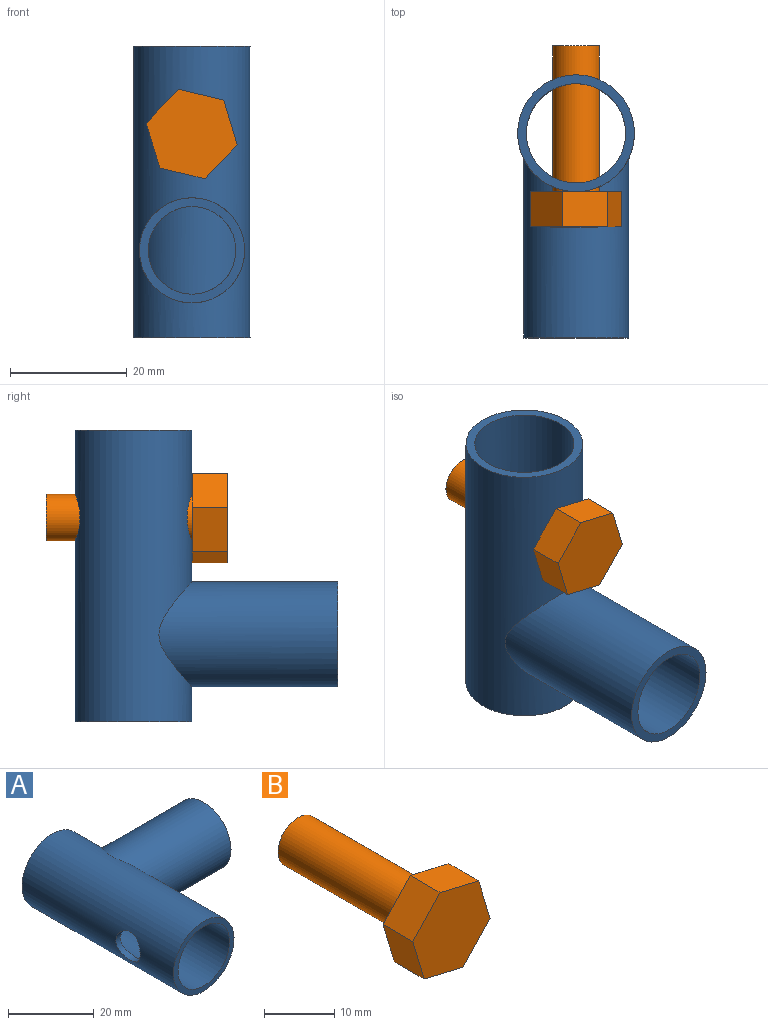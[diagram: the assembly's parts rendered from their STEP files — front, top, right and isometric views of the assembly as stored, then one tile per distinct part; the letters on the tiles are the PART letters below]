
ASSEMBLY  parts=2 mates=1
PART A: 10 faces, bbox 45x50x20 mm
  f0: cylinder r=10mm len=50mm, axis (0,1,0), area 2744.7mm2, adj f2,f3,f5,f8,f9
  f1: cylinder r=8.5mm len=50mm, axis (0,1,0), area 2566.7mm2, adj f2,f3,f8,f9
  f2: plane 20x20mm, normal (0,-1,0), area 87.2mm2, adj f0,f1
  f3: plane 20x20mm, normal (0,1,0), area 87.2mm2, adj f0,f1
  f4: plane 18x18mm, normal (1,0,0), area 77.8mm2, adj f5,f6
  f5: cylinder r=9mm len=30.66mm, axis (-1,0,0), area 1558.3mm2, adj f0,f4
  f6: cylinder r=7.5mm len=28.4mm, axis (-1,0,0), area 1254.3mm2, adj f4,f7
  f7: cylinder r=10mm len=15mm, axis (0,1,0), area 193mm2, adj f6
  f8: cylinder r=4mm len=8mm, axis (1,0,0), area 39.3mm2, adj f0,f1
  f9: cylinder r=4mm len=8mm, axis (1,0,0), area 40mm2, adj f0,f1
PART B: 10 faces, bbox 15.6x31x15.3 mm
  f0: plane 7.67x6mm, normal (0.96,0,0.29), area 48mm2, adj f1,f5,f6,f7
  f1: plane 7.78x6mm, normal (0.23,0,0.97), area 48mm2, adj f0,f2,f6,f7
  f2: plane 6x5.81mm, normal (-0.73,0,0.69), area 48mm2, adj f1,f3,f6,f7
  f3: plane 7.67x6mm, normal (-0.96,0,-0.29), area 48mm2, adj f2,f4,f6,f7
  f4: plane 7.78x6mm, normal (-0.23,0,-0.97), area 48mm2, adj f3,f5,f6,f7
  f5: plane 6x5.81mm, normal (0.73,0,-0.69), area 48mm2, adj f0,f4,f6,f7
  f6: plane 15.56x15.33mm, normal (0,-1,0), area 166.3mm2, adj f0,f1,f2,f3,f4,f5
  f7: plane 15.56x15.33mm, normal (0,1,0), area 116mm2, adj f0,f1,f2,f3,f4,f5,f8
  f8: cylinder r=4mm len=25mm, axis (0,-1,0), area 628.3mm2, adj f7,f9
  f9: plane 8x8mm, normal (0,1,0), area 50.3mm2, adj f8
PLACE A rot(axis=(-0.58,0.58,-0.58),120deg) t=(17.9,-103.36,-56.12)mm
PLACE B t=(-42.67,-113.37,-127.84)mm
MATE fastened A.f8 <-> B.f8  axis (0,-1,0) through (17.9,-113.37,-21.12)mm
